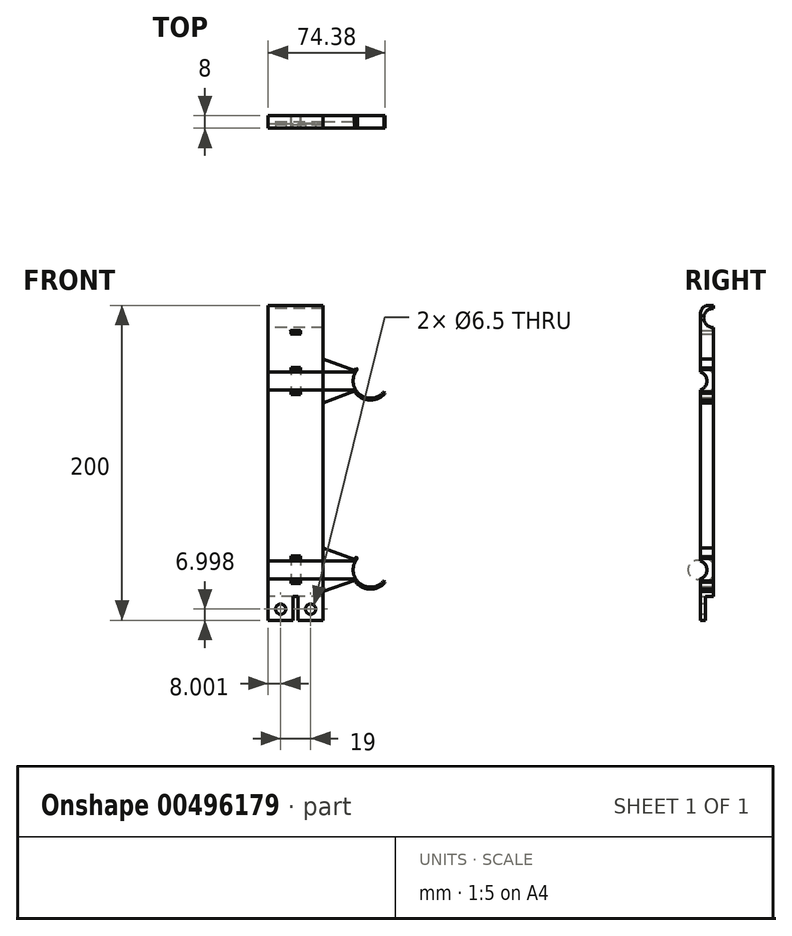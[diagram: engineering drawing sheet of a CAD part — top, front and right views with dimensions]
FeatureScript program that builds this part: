
annotation { "Feature Type Name" : "Feature", "Feature Type Description" : "" }
export const myFeature = defineFeature(function(context is Context, id is Id, definition is map)
    precondition{}
    {
        {
            var Q0;
            Q0=qCreatedBy(makeId("Front.planeOp"),FACE);
            var sketch = newSketch(context, id + "F0", { "sketchPlane" : qUnion([Q0])});
            skLineSegment(sketch, "E0.bottom", {"start": v(-13.38, 145.24) * mm, "end": v(21.62, 145.24) * mm});
            skLineSegment(sketch, "E0.top", {"start": v(-13.38, -54.76) * mm, "end": v(21.62, -54.76) * mm});
            skLineSegment(sketch, "E0.left", {"start": v(-13.38, 145.24) * mm, "end": v(-13.38, -54.76) * mm});
            skLineSegment(sketch, "E0.right", {"start": v(21.62, 145.24) * mm, "end": v(21.62, -54.76) * mm});
            skLineSegment(sketch, "E1", {"start": v(21.62, 145.24) * mm, "end": v(21.62, 137.24) * mm, "construction": true});
            skLineSegment(sketch, "E2", {"start": v(21.62, 137.24) * mm, "end": v(-13.38, 137.24) * mm, "construction": true});
            skSolve(sketch);
        }
        {
            var Q0;
            Q0=makeQuery(id+"F0.imprint","IMPRINT",FACE,{"disambiguationData":[TD([[makeQuery(id+"F0.imprint","IMPRINT",EDGE,{"derivedFrom":sQuery(id+"F0.wireOp",EDGE,"E0.bottom")}),-1.0]])]});
            extrude(context, id + "F1", {"entities" : qUnion([Q0]), "depth" : 8 * mm});
        }
        {
            var Q0;
            Q0=makeQuery(id+"F1.opExtrude","SWEPT_FACE",FACE,{"disambiguationData":[OSD([sQuery(id+"F0.wireOp",EDGE,"E0.left")])]});
            var sketch = newSketch(context, id + "F2", { "sketchPlane" : qUnion([Q0])});
            skLineSegment(sketch, "E3", {"start": v(0, 145.24) * mm, "end": v(0, 137.24) * mm, "construction": true});
            skLineSegment(sketch, "E4", {"start": v(0, 137.24) * mm, "end": v(-10.7, 137.24) * mm, "construction": true});
            skCircle(sketch, "E5", {"center": v(0, 137.24) * mm, "radius": 6.08 * mm, "construction": true});
            skCircle(sketch, "E6", {"center": v(0, 137.24) * mm, "radius": 6.08 * mm});
            skSolve(sketch);
        }
        {
            var Q0;
            Q0=qSketchRegion(id+"F2",true);
            extrude(context, id + "F3", {"entities" : qUnion([Q0]), "operationType" : NewBodyOperationType.REMOVE, "oppositeDirection" : true, "depth" : 45 * mm});
        }
        {
            var Q0;
            {var subQ0=sQuery(id+"F0.wireOp",EDGE,"E0.top");var subQ1=sQuery(id+"F0.wireOp",EDGE,"E0.left");var subQ2=sQuery(id+"F0.wireOp",EDGE,"E0.right");Q0=makeQuery(id+"F3.boolean.opBoolean","SPLIT",FACE,{"disambiguationData":[TD([makeQuery(id+"F1.opExtrude","SWEPT_FACE",FACE,{"disambiguationData":[OSD([subQ0])]})])],"derivedFrom":makeQuery(id+"F1.opExtrude","CAP_FACE",FACE,{"disambiguationData":[OSD([sQuery(id+"F0.wireOp",EDGE,"E0.bottom"),subQ0,subQ1,subQ2])],"isStart":true})});}
            var sketch = newSketch(context, id + "F4", { "sketchPlane" : qUnion([Q0])});
            skLineSegment(sketch, "E7", {"start": v(-4.12, 129.16) * mm, "end": v(-1.12, 129.16) * mm, "construction": true});
            skLineSegment(sketch, "E8", {"start": v(-1.12, 129.16) * mm, "end": v(-7.12, 129.16) * mm, "construction": true});
            skLineSegment(sketch, "E9.bottom", {"start": v(-7.12, 129.16) * mm, "end": v(-1.12, 129.16) * mm});
            skLineSegment(sketch, "E9.top", {"start": v(-7.12, 127.16) * mm, "end": v(-1.12, 127.16) * mm});
            skLineSegment(sketch, "E9.left", {"start": v(-7.12, 129.16) * mm, "end": v(-7.12, 127.16) * mm});
            skLineSegment(sketch, "E9.right", {"start": v(-1.12, 129.16) * mm, "end": v(-1.12, 127.16) * mm});
            skSolve(sketch);
        }
        {
            var Q0;
            Q0=makeQuery(id+"F4.imprint","IMPRINT",FACE,{"disambiguationData":[TD([[makeQuery(id+"F4.imprint","IMPRINT",EDGE,{"derivedFrom":sQuery(id+"F4.wireOp",EDGE,"E9.bottom")}),-1.0]])]});
            var sketch = newSketch(context, id + "F5", { "sketchPlane" : qUnion([Q0])});
            skSolve(sketch);
        }
        {
            var Q0;
            Q0=qSketchRegion(id+"F5",true);
            var Q1;
            Q1=makeQuery(id+"F4.imprint","IMPRINT",FACE,{"disambiguationData":[TD([[makeQuery(id+"F4.imprint","IMPRINT",EDGE,{"derivedFrom":sQuery(id+"F4.wireOp",EDGE,"E9.bottom")}),-1.0]])]});
            extrude(context, id + "F6", {"entities" : qUnion([Q0, Q1]), "operationType" : NewBodyOperationType.REMOVE, "oppositeDirection" : true, "depth" : 25 * mm});
        }
        {
            var Q0;
            Q0=makeQuery(id+"F6.boolean.opBoolean","INTERSECT",EDGE,{"derivedFrom":[makeQuery(id+"F1.opExtrude","CAP_FACE",FACE,{"disambiguationData":[OSD([sQuery(id+"F0.wireOp",EDGE,"E0.bottom"),sQuery(id+"F0.wireOp",EDGE,"E0.top"),sQuery(id+"F0.wireOp",EDGE,"E0.left"),sQuery(id+"F0.wireOp",EDGE,"E0.right")])],"isStart":false}),makeQuery(id+"F6.opExtrude","SWEPT_FACE",FACE,{"disambiguationData":[OSD([sQuery(id+"F4.wireOp",EDGE,"E9.bottom")])]})]});
            var Q1;
            Q1=makeQuery(id+"F6.boolean.opBoolean","INTERSECT",EDGE,{"derivedFrom":[makeQuery(id+"F1.opExtrude","CAP_FACE",FACE,{"disambiguationData":[OSD([sQuery(id+"F0.wireOp",EDGE,"E0.bottom"),sQuery(id+"F0.wireOp",EDGE,"E0.top"),sQuery(id+"F0.wireOp",EDGE,"E0.left"),sQuery(id+"F0.wireOp",EDGE,"E0.right")])],"isStart":false}),makeQuery(id+"F6.opExtrude","SWEPT_FACE",FACE,{"disambiguationData":[OSD([sQuery(id+"F4.wireOp",EDGE,"E9.top")])]})]});
            var Q2;
            Q2=makeQuery(id+"F6.boolean.opBoolean","INTERSECT",EDGE,{"derivedFrom":[makeQuery(id+"F1.opExtrude","CAP_FACE",FACE,{"disambiguationData":[OSD([sQuery(id+"F0.wireOp",EDGE,"E0.bottom"),sQuery(id+"F0.wireOp",EDGE,"E0.top"),sQuery(id+"F0.wireOp",EDGE,"E0.left"),sQuery(id+"F0.wireOp",EDGE,"E0.right")])],"isStart":false}),makeQuery(id+"F6.opExtrude","SWEPT_FACE",FACE,{"disambiguationData":[OSD([sQuery(id+"F4.wireOp",EDGE,"E9.left")])]})]});
            var Q3;
            Q3=makeQuery(id+"F6.boolean.opBoolean","INTERSECT",EDGE,{"derivedFrom":[makeQuery(id+"F1.opExtrude","CAP_FACE",FACE,{"disambiguationData":[OSD([sQuery(id+"F0.wireOp",EDGE,"E0.bottom"),sQuery(id+"F0.wireOp",EDGE,"E0.top"),sQuery(id+"F0.wireOp",EDGE,"E0.left"),sQuery(id+"F0.wireOp",EDGE,"E0.right")])],"isStart":false}),makeQuery(id+"F6.opExtrude","SWEPT_FACE",FACE,{"disambiguationData":[OSD([sQuery(id+"F4.wireOp",EDGE,"E9.right")])]})]});
            var Q4;
            Q4=makeQuery(id+"F6.boolean.opBoolean","COPY",EDGE,{"derivedFrom":makeQuery(id+"F6.opExtrude","CAP_EDGE",EDGE,{"disambiguationData":[OSD([sQuery(id+"F4.wireOp",EDGE,"E9.bottom")])],"isStart":true})});
            var Q5;
            Q5=makeQuery(id+"F6.boolean.opBoolean","COPY",EDGE,{"derivedFrom":makeQuery(id+"F6.opExtrude","CAP_EDGE",EDGE,{"disambiguationData":[OSD([sQuery(id+"F4.wireOp",EDGE,"E9.left")])],"isStart":true})});
            var Q6;
            Q6=makeQuery(id+"F6.boolean.opBoolean","COPY",EDGE,{"derivedFrom":makeQuery(id+"F6.opExtrude","CAP_EDGE",EDGE,{"disambiguationData":[OSD([sQuery(id+"F4.wireOp",EDGE,"E9.top")])],"isStart":true})});
            var Q7;
            Q7=makeQuery(id+"F6.boolean.opBoolean","COPY",EDGE,{"derivedFrom":makeQuery(id+"F6.opExtrude","CAP_EDGE",EDGE,{"disambiguationData":[OSD([sQuery(id+"F4.wireOp",EDGE,"E9.right")])],"isStart":true})});
            fillet(context, id + "F7", {"entities" : qUnion([Q0, Q1, Q2, Q3, Q4, Q5, Q6, Q7]), "radius" : 0.3 * mm, "tangentPropagation" : true, "allowEdgeOverflow" : false});
        }
        {
            var Q0;
            Q0=makeQuery(id+"F1.opExtrude","CAP_FACE",FACE,{"disambiguationData":[OSD([sQuery(id+"F0.wireOp",EDGE,"E0.bottom"),sQuery(id+"F0.wireOp",EDGE,"E0.top"),sQuery(id+"F0.wireOp",EDGE,"E0.left"),sQuery(id+"F0.wireOp",EDGE,"E0.right")])],"isStart":false});
            var sketch = newSketch(context, id + "F8", { "sketchPlane" : qUnion([Q0])});
            skLineSegment(sketch, "E10", {"start": v(-13.38, 145.24) * mm, "end": v(-13.38, -47.76) * mm, "construction": true});
            skLineSegment(sketch, "E11", {"start": v(-13.38, -47.76) * mm, "end": v(82.12, -47.76) * mm, "construction": true});
            skLineSegment(sketch, "E12", {"start": v(-13.38, -47.76) * mm, "end": v(21.62, -47.76) * mm, "construction": true});
            skLineSegment(sketch, "E13", {"start": v(21.62, -47.76) * mm, "end": v(13.62, -47.76) * mm, "construction": true});
            skLineSegment(sketch, "E14", {"start": v(13.62, -47.76) * mm, "end": v(13.62, -34.39) * mm, "construction": true});
            skLineSegment(sketch, "E15", {"start": v(-13.38, -47.76) * mm, "end": v(-5.38, -47.76) * mm, "construction": true});
            skLineSegment(sketch, "E16", {"start": v(-5.38, -43.12) * mm, "end": v(-5.38, -47.76) * mm, "construction": true});
            skCircle(sketch, "E17", {"center": v(-5.38, -47.76) * mm, "radius": 3.25 * mm});
            skCircle(sketch, "E18", {"center": v(13.62, -47.76) * mm, "radius": 3.25 * mm});
            skSolve(sketch);
        }
        {
            var Q0;
            Q0=qSketchRegion(id+"F8",true);
            extrude(context, id + "F9", {"entities" : qUnion([Q0]), "operationType" : NewBodyOperationType.REMOVE, "oppositeDirection" : true, "depth" : 25 * mm});
        }
        {
            var Q0;
            {var subQ0=sQuery(id+"F0.wireOp",EDGE,"E0.top");var subQ1=sQuery(id+"F0.wireOp",EDGE,"E0.left");var subQ2=sQuery(id+"F0.wireOp",EDGE,"E0.right");Q0=makeQuery(id+"F3.boolean.opBoolean","SPLIT",FACE,{"disambiguationData":[TD([makeQuery(id+"F1.opExtrude","SWEPT_FACE",FACE,{"disambiguationData":[OSD([subQ0])]})])],"derivedFrom":makeQuery(id+"F1.opExtrude","CAP_FACE",FACE,{"disambiguationData":[OSD([sQuery(id+"F0.wireOp",EDGE,"E0.bottom"),subQ0,subQ1,subQ2])],"isStart":true})});}
            var sketch = newSketch(context, id + "F10", { "sketchPlane" : qUnion([Q0])});
            skLineSegment(sketch, "E19.bottom", {"start": v(-21.62, -54.76) * mm, "end": v(13.38, -54.76) * mm});
            skLineSegment(sketch, "E19.top", {"start": v(-21.62, -39.76) * mm, "end": v(13.38, -39.76) * mm});
            skLineSegment(sketch, "E19.left", {"start": v(-21.62, -54.76) * mm, "end": v(-21.62, -39.76) * mm});
            skLineSegment(sketch, "E19.right", {"start": v(13.38, -54.76) * mm, "end": v(13.38, -39.76) * mm});
            skSolve(sketch);
        }
        {
            var Q0;
            Q0=makeQuery(id+"F10.imprint","IMPRINT",FACE,{"disambiguationData":[TD([[makeQuery(id+"F10.imprint","IMPRINT",EDGE,{"derivedFrom":sQuery(id+"F10.wireOp",EDGE,"E19.bottom")}),-1.0]])]});
            extrude(context, id + "F11", {"entities" : qUnion([Q0]), "operationType" : NewBodyOperationType.REMOVE, "oppositeDirection" : true, "depth" : 5 * mm});
        }
        {
            var Q0;
            Q0=makeQuery(id+"F11.boolean.opBoolean","COPY",FACE,{"derivedFrom":makeQuery(id+"F11.opExtrude","CAP_FACE",FACE,{"disambiguationData":[OSD([sQuery(id+"F0.wireOp",EDGE,"E0.bottom"),sQuery(id+"F0.wireOp",EDGE,"E0.top"),sQuery(id+"F0.wireOp",EDGE,"E0.left"),sQuery(id+"F0.wireOp",EDGE,"E0.right"),sQuery(id+"F8.wireOp",EDGE,"E17"),sQuery(id+"F8.wireOp",EDGE,"E18"),sQuery(id+"F10.wireOp",EDGE,"E19.bottom"),sQuery(id+"F10.wireOp",EDGE,"E19.top"),sQuery(id+"F10.wireOp",EDGE,"E19.left"),sQuery(id+"F10.wireOp",EDGE,"E19.right")])],"isStart":false})});
            var sketch = newSketch(context, id + "F12", { "sketchPlane" : qUnion([Q0])});
            skLineSegment(sketch, "E20", {"start": v(-21.62, -54.76) * mm, "end": v(-7.62, -54.76) * mm, "construction": true});
            skLineSegment(sketch, "E21", {"start": v(-5.72, -39.76) * mm, "end": v(-5.72, -54.76) * mm, "construction": true});
            skLineSegment(sketch, "E22", {"start": v(-2.52, -54.76) * mm, "end": v(-2.52, -39.76) * mm, "construction": true});
            skLineSegment(sketch, "E23.right", {"start": v(-5.72, -54.76) * mm, "end": v(-5.72, -39.76) * mm});
            skLineSegment(sketch, "E24.left", {"start": v(-2.52, -54.76) * mm, "end": v(-2.52, -39.76) * mm});
            skLineSegment(sketch, "E25.top", {"start": v(-2.52, -54.76) * mm, "end": v(-5.72, -54.76) * mm});
            skLineSegment(sketch, "E25.left", {"start": v(-2.52, -39.76) * mm, "end": v(-2.52, -54.76) * mm});
            skLineSegment(sketch, "E25.right", {"start": v(-5.72, -39.76) * mm, "end": v(-5.72, -54.76) * mm});
            skPoint(sketch, "E26.end.orphan", {"position": v(-0.62, -54.76) * mm});
            skLineSegment(sketch, "E27.top", {"start": v(-21.62, -54.76) * mm, "end": v(-5.72, -54.76) * mm});
            skLineSegment(sketch, "E28.bottom", {"start": v(-2.52, -39.76) * mm, "end": v(13.38, -39.76) * mm});
            skLineSegment(sketch, "E28.top", {"start": v(-2.52, -54.76) * mm, "end": v(-0.62, -54.76) * mm});
            skLineSegment(sketch, "E29.bottom", {"start": v(-5.72, -39.76) * mm, "end": v(-2.52, -39.76) * mm});
            skLineSegment(sketch, "E29.top", {"start": v(-5.72, -54.76) * mm, "end": v(-2.52, -54.76) * mm});
            skSolve(sketch);
        }
        {
            var Q0;
            Q0 = qSketchRegion(id + "F12", true);
            var Q1;
            {var subQ0=sQuery(id+"F0.wireOp",EDGE,"E0.top");var subQ1=sQuery(id+"F0.wireOp",EDGE,"E0.left");var subQ2=sQuery(id+"F0.wireOp",EDGE,"E0.right");Q1=makeQuery(id+"F3.boolean.opBoolean","SPLIT",FACE,{"disambiguationData":[TD([makeQuery(id+"F1.opExtrude","SWEPT_FACE",FACE,{"disambiguationData":[OSD([subQ0])]})])],"derivedFrom":makeQuery(id+"F1.opExtrude","CAP_FACE",FACE,{"disambiguationData":[OSD([sQuery(id+"F0.wireOp",EDGE,"E0.bottom"),subQ0,subQ1,subQ2])],"isStart":true})});}
            extrude(context, id + "F13", {"entities" : qUnion([Q0]), "operationType" : NewBodyOperationType.REMOVE, "oppositeDirection" : true, "endBoundEntityFace" : qUnion([Q1]), "depth" : 5 * mm});
        }
        {
            var Q0;
            Q0=makeQuery(id+"F1.opExtrude","CAP_FACE",FACE,{"disambiguationData":[OSD([sQuery(id+"F0.wireOp",EDGE,"E0.bottom"),sQuery(id+"F0.wireOp",EDGE,"E0.top"),sQuery(id+"F0.wireOp",EDGE,"E0.left"),sQuery(id+"F0.wireOp",EDGE,"E0.right")])],"isStart":false});
            var sketch = newSketch(context, id + "F14", { "sketchPlane" : qUnion([Q0])});
            skLineSegment(sketch, "E30", {"start": v(21.62, 145.24) * mm, "end": v(21.62, 97.24) * mm, "construction": true});
            skLineSegment(sketch, "E31", {"start": v(21.62, 97.24) * mm, "end": v(-44.16, 97.24) * mm, "construction": true});
            skLineSegment(sketch, "E32", {"start": v(21.62, 97.24) * mm, "end": v(51.62, 97.24) * mm, "construction": true});
            skLineSegment(sketch, "E33", {"start": v(51.62, 97.24) * mm, "end": v(51.62, 86.24) * mm, "construction": true});
            skArc(sketch, "E34", {"start": v(43.4, 104.54) * mm, "mid": v(44.46, 88.9) * mm, "end": v(60.09, 90.22) * mm, "construction": true});
            skArc(sketch, "E35.0", {"start": v(42.53, 105.29) * mm, "mid": v(41.92, 104.54) * mm, "end": v(41.37, 103.74) * mm});
            skLineSegment(sketch, "E36", {"start": v(41.37, 103.74) * mm, "end": v(21.62, 111.24) * mm});
            skLineSegment(sketch, "E37", {"start": v(21.62, 111.24) * mm, "end": v(21.62, 26.35) * mm});
            skArc(sketch, "E38", {"start": v(43.4, 104.54) * mm, "mid": v(44.46, 88.9) * mm, "end": v(60.09, 90.22) * mm});
            skLineSegment(sketch, "E39.MirrorCS", {"start": v(41.37, 90.74) * mm, "end": v(21.62, 83.24) * mm});
            skLineSegment(sketch, "E40", {"start": v(42.53, 105.29) * mm, "end": v(43.4, 104.54) * mm});
            skArc(sketch, "E41.trimOffspring", {"start": v(41.37, 90.74) * mm, "mid": v(50.84, 85.12) * mm, "end": v(60.96, 89.48) * mm});
            skLineSegment(sketch, "E42.trimOffspring", {"start": v(60.09, 90.22) * mm, "end": v(60.96, 89.48) * mm});
            skSolve(sketch);
        }
        {
            var Q0;
            Q0=makeQuery(id+"F14.imprint","IMPRINT",FACE,{"disambiguationData":[TD([[makeQuery(id+"F14.imprint","IMPRINT",EDGE,{"derivedFrom":sQuery(id+"F14.wireOp",EDGE,"E35.0")}),1.0]])]});
            extrude(context, id + "F15", {"entities" : qUnion([Q0]), "oppositeDirection" : true, "depth" : 8 * mm});
        }
        {
            var Q0;
            Q0=makeQuery(id+"F1.opExtrude","SWEPT_FACE",FACE,{"disambiguationData":[OSD([sQuery(id+"F0.wireOp",EDGE,"E0.left")])]});
            var sketch = newSketch(context, id + "F16", { "sketchPlane" : qUnion([Q0])});
            skLineSegment(sketch, "E43", {"start": v(10, 97.24) * mm, "end": v(37.36, 97.24) * mm, "construction": true});
            skCircle(sketch, "E44", {"center": v(10, 97.24) * mm, "radius": 6 * mm});
            skSolve(sketch);
        }
        {
            var Q0;
            {var subQ0=sQuery(id+"F16.wireOp",EDGE,"E44");var subQ1=makeQuery(id+"F1.opExtrude","CAP_EDGE",EDGE,{"disambiguationData":[OSD([sQuery(id+"F0.wireOp",EDGE,"E0.left")])],"isStart":false});var subQ2=makeQuery(id+"F16.imprint","INTERSECT",VERTEX,{"disambiguationData":[OD(0.0)],"derivedFrom":[subQ1,subQ0]});Q0=makeQuery(id+"F16.imprint","IMPRINT",FACE,{"disambiguationData":[TD([[makeQuery(id+"F16.imprint","IMPRINT",EDGE,{"disambiguationData":[TD([[subQ2,-1.0]])],"derivedFrom":subQ0}),1.0]])]});}
            var Q1;
            Q1=makeQuery(id+"F15.opExtrude","SWEPT_FACE",FACE,{"disambiguationData":[OSD([sQuery(id+"F14.wireOp",EDGE,"E38")])]});
            extrude(context, id + "F17", {"entities" : qUnion([Q0]), "operationType" : NewBodyOperationType.REMOVE, "oppositeDirection" : true, "endBoundEntityFace" : qUnion([Q1]), "depth" : 60 * mm});
        }
        {
            var Q0;
            {var subQ0=sQuery(id+"F0.wireOp",EDGE,"E0.right");var subQ1=sQuery(id+"F0.wireOp",EDGE,"E0.left");var subQ2=sQuery(id+"F0.wireOp",EDGE,"E0.top");Q0=makeQuery(id+"F17.boolean.opBoolean","SPLIT",FACE,{"disambiguationData":[TD([makeQuery(id+"F1.opExtrude","SWEPT_FACE",FACE,{"disambiguationData":[OSD([subQ2])]})])],"derivedFrom":makeQuery(id+"F1.opExtrude","CAP_FACE",FACE,{"disambiguationData":[OSD([sQuery(id+"F0.wireOp",EDGE,"E0.bottom"),subQ2,subQ1,subQ0])],"isStart":false})});}
            var sketch = newSketch(context, id + "F18", { "sketchPlane" : qUnion([Q0])});
            skLineSegment(sketch, "E45.bottom", {"start": v(1.12, 105.9) * mm, "end": v(7.12, 105.9) * mm});
            skLineSegment(sketch, "E45.top", {"start": v(1.12, 103.9) * mm, "end": v(7.12, 103.9) * mm});
            skLineSegment(sketch, "E45.left", {"start": v(1.12, 105.9) * mm, "end": v(1.12, 103.9) * mm});
            skLineSegment(sketch, "E45.right", {"start": v(7.12, 105.9) * mm, "end": v(7.12, 103.9) * mm});
            skLineSegment(sketch, "E46.bottom", {"start": v(1.12, 90.58) * mm, "end": v(7.12, 90.58) * mm});
            skLineSegment(sketch, "E46.top", {"start": v(1.12, 88.58) * mm, "end": v(7.12, 88.58) * mm});
            skLineSegment(sketch, "E46.left", {"start": v(1.12, 90.58) * mm, "end": v(1.12, 88.58) * mm});
            skLineSegment(sketch, "E46.right", {"start": v(7.12, 90.58) * mm, "end": v(7.12, 88.58) * mm});
            skSolve(sketch);
        }
        {
            var Q0;
            Q0=makeQuery(id+"F18.imprint","IMPRINT",FACE,{"disambiguationData":[TD([[makeQuery(id+"F18.imprint","IMPRINT",EDGE,{"derivedFrom":sQuery(id+"F18.wireOp",EDGE,"E45.bottom")}),-1.0]])]});
            var Q1;
            Q1=makeQuery(id+"F18.imprint","IMPRINT",FACE,{"disambiguationData":[TD([[makeQuery(id+"F18.imprint","IMPRINT",EDGE,{"derivedFrom":sQuery(id+"F18.wireOp",EDGE,"E46.bottom")}),-1.0]])]});
            extrude(context, id + "F19", {"entities" : qUnion([Q0, Q1]), "operationType" : NewBodyOperationType.REMOVE, "oppositeDirection" : true, "depth" : 25 * mm});
        }
        {
            var Q0;
            {var subQ0=sQuery(id+"F0.wireOp",EDGE,"E0.top");var subQ1=sQuery(id+"F0.wireOp",EDGE,"E0.left");var subQ2=sQuery(id+"F0.wireOp",EDGE,"E0.right");Q0=makeQuery(id+"F19.boolean.opBoolean","INTERSECT",EDGE,{"derivedFrom":[makeQuery(id+"F3.boolean.opBoolean","SPLIT",FACE,{"disambiguationData":[TD([makeQuery(id+"F1.opExtrude","SWEPT_FACE",FACE,{"disambiguationData":[OSD([subQ0])]})])],"derivedFrom":makeQuery(id+"F1.opExtrude","CAP_FACE",FACE,{"disambiguationData":[OSD([sQuery(id+"F0.wireOp",EDGE,"E0.bottom"),subQ0,subQ1,subQ2])],"isStart":true})}),makeQuery(id+"F19.opExtrude","SWEPT_FACE",FACE,{"disambiguationData":[OSD([sQuery(id+"F18.wireOp",EDGE,"E45.top")])]})]});}
            var Q1;
            {var subQ0=sQuery(id+"F0.wireOp",EDGE,"E0.top");var subQ1=sQuery(id+"F0.wireOp",EDGE,"E0.left");var subQ2=sQuery(id+"F0.wireOp",EDGE,"E0.right");Q1=makeQuery(id+"F19.boolean.opBoolean","INTERSECT",EDGE,{"derivedFrom":[makeQuery(id+"F3.boolean.opBoolean","SPLIT",FACE,{"disambiguationData":[TD([makeQuery(id+"F1.opExtrude","SWEPT_FACE",FACE,{"disambiguationData":[OSD([subQ0])]})])],"derivedFrom":makeQuery(id+"F1.opExtrude","CAP_FACE",FACE,{"disambiguationData":[OSD([sQuery(id+"F0.wireOp",EDGE,"E0.bottom"),subQ0,subQ1,subQ2])],"isStart":true})}),makeQuery(id+"F19.opExtrude","SWEPT_FACE",FACE,{"disambiguationData":[OSD([sQuery(id+"F18.wireOp",EDGE,"E46.bottom")])]})]});}
            fillet(context, id + "F20", {"entities" : qUnion([Q0, Q1]), "radius" : 3 * mm, "tangentPropagation" : true, "allowEdgeOverflow" : false});
        }
        {
            var Q0;
            {var subQ0=sQuery(id+"F0.wireOp",EDGE,"E0.left");var subQ1=sQuery(id+"F0.wireOp",EDGE,"E0.right");var subQ2=sQuery(id+"F0.wireOp",EDGE,"E0.top");var subQ3=sQuery(id+"F0.wireOp",EDGE,"E0.bottom");Q0=makeQuery(id+"F17.boolean.opBoolean","SPLIT",FACE,{"disambiguationData":[TD([makeQuery(id+"F1.opExtrude","SWEPT_FACE",FACE,{"disambiguationData":[OSD([subQ3])]})])],"derivedFrom":makeQuery(id+"F1.opExtrude","CAP_FACE",FACE,{"disambiguationData":[OSD([subQ3,subQ2,subQ0,subQ1])],"isStart":false})});}
            var sketch = newSketch(context, id + "F21", { "sketchPlane" : qUnion([Q0])});
            skLineSegment(sketch, "E47", {"start": v(21.62, 145.24) * mm, "end": v(21.62, -22.76) * mm, "construction": true});
            skLineSegment(sketch, "E48", {"start": v(21.62, -22.76) * mm, "end": v(-13.38, -22.76) * mm, "construction": true});
            skLineSegment(sketch, "E49", {"start": v(21.62, -22.78) * mm, "end": v(51.62, -22.78) * mm, "construction": true});
            skLineSegment(sketch, "E50", {"start": v(51.62, -22.78) * mm, "end": v(51.62, -33.78) * mm, "construction": true});
            skArc(sketch, "E51", {"start": v(43.4, -15.47) * mm, "mid": v(44.46, -31.12) * mm, "end": v(60.09, -29.8) * mm, "construction": true});
            skArc(sketch, "E52.0", {"start": v(42.49, -14.69) * mm, "mid": v(41.9, -15.4) * mm, "end": v(41.37, -16.17) * mm});
            skLineSegment(sketch, "E53", {"start": v(41.37, -16.17) * mm, "end": v(21.62, -8.94) * mm});
            skLineSegment(sketch, "E54", {"start": v(21.62, -8.94) * mm, "end": v(21.62, -43.66) * mm});
            skArc(sketch, "E55", {"start": v(43.4, -15.47) * mm, "mid": v(44.46, -31.12) * mm, "end": v(60.09, -29.8) * mm});
            skLineSegment(sketch, "E56.MirrorCS", {"start": v(41.37, -29.39) * mm, "end": v(21.62, -36.62) * mm});
            skLineSegment(sketch, "E57", {"start": v(42.49, -14.69) * mm, "end": v(43.4, -15.47) * mm});
            skArc(sketch, "E58.trimOffspring", {"start": v(41.37, -29.39) * mm, "mid": v(50.88, -34.95) * mm, "end": v(61, -30.58) * mm});
            skLineSegment(sketch, "E59.trimOffspring", {"start": v(60.09, -29.8) * mm, "end": v(61, -30.58) * mm});
            skSolve(sketch);
        }
        {
            var Q0;
            Q0=makeQuery(id+"F21.imprint","IMPRINT",FACE,{"disambiguationData":[TD([[makeQuery(id+"F21.imprint","IMPRINT",EDGE,{"derivedFrom":sQuery(id+"F21.wireOp",EDGE,"E52.0")}),1.0]])]});
            extrude(context, id + "F22", {"entities" : qUnion([Q0]), "oppositeDirection" : true, "depth" : 8 * mm});
        }
        {
            var Q0;
            Q0=makeQuery(id+"F1.opExtrude","SWEPT_FACE",FACE,{"disambiguationData":[OSD([sQuery(id+"F0.wireOp",EDGE,"E0.left")])]});
            var sketch = newSketch(context, id + "F23", { "sketchPlane" : qUnion([Q0])});
            skCircle(sketch, "E60", {"center": v(10, -22.76) * mm, "radius": 6 * mm});
            skSolve(sketch);
        }
        {
            var Q0;
            {var subQ0=sQuery(id+"F23.wireOp",EDGE,"E60");var subQ1=sQuery(id+"F0.wireOp",EDGE,"E0.left");var subQ2=sQuery(id+"F0.wireOp",EDGE,"E0.top");var subQ3=makeQuery(id+"F17.boolean.opBoolean","SPLIT",EDGE,{"disambiguationData":[TD([makeQuery(id+"F1.opExtrude","SWEPT_FACE",FACE,{"disambiguationData":[OSD([subQ2])]})])],"derivedFrom":makeQuery(id+"F1.opExtrude","CAP_EDGE",EDGE,{"disambiguationData":[OSD([subQ1])],"isStart":false})});var subQ4=makeQuery(id+"F23.imprint","INTERSECT",VERTEX,{"disambiguationData":[OD(0.0)],"derivedFrom":[subQ3,subQ0]});Q0=makeQuery(id+"F23.imprint","IMPRINT",FACE,{"disambiguationData":[TD([[makeQuery(id+"F23.imprint","IMPRINT",EDGE,{"disambiguationData":[TD([[subQ4,1.0]])],"derivedFrom":subQ0}),1.0]])]});}
            extrude(context, id + "F24", {"entities" : qUnion([Q0]), "operationType" : NewBodyOperationType.REMOVE, "oppositeDirection" : true, "depth" : 60 * mm});
        }
        {
            var Q0;
            {var subQ0=sQuery(id+"F0.wireOp",EDGE,"E0.right");var subQ1=sQuery(id+"F0.wireOp",EDGE,"E0.left");var subQ2=sQuery(id+"F0.wireOp",EDGE,"E0.top");var subQ3=makeQuery(id+"F1.opExtrude","CAP_FACE",FACE,{"disambiguationData":[OSD([sQuery(id+"F0.wireOp",EDGE,"E0.bottom"),subQ2,subQ1,subQ0])],"isStart":false});Q0=makeQuery(id+"F24.boolean.opBoolean","SPLIT",FACE,{"disambiguationData":[TD([makeQuery(id+"F19.boolean.opBoolean","COPY",FACE,{"derivedFrom":makeQuery(id+"F19.opExtrude","SWEPT_FACE",FACE,{"disambiguationData":[OSD([sQuery(id+"F18.wireOp",EDGE,"E46.bottom")])]})})])],"derivedFrom":makeQuery(id+"F17.boolean.opBoolean","SPLIT",FACE,{"disambiguationData":[TD([makeQuery(id+"F1.opExtrude","SWEPT_FACE",FACE,{"disambiguationData":[OSD([subQ2])]})])],"derivedFrom":subQ3})});}
            var sketch = newSketch(context, id + "F25", { "sketchPlane" : qUnion([Q0])});
            skLineSegment(sketch, "E61.bottom", {"start": v(1.12, -14.1) * mm, "end": v(7.12, -14.1) * mm});
            skLineSegment(sketch, "E61.top", {"start": v(1.12, -16.1) * mm, "end": v(7.12, -16.1) * mm});
            skLineSegment(sketch, "E61.left", {"start": v(1.12, -14.1) * mm, "end": v(1.12, -16.1) * mm});
            skLineSegment(sketch, "E61.right", {"start": v(7.12, -14.1) * mm, "end": v(7.12, -16.1) * mm});
            skLineSegment(sketch, "E62.bottom", {"start": v(1.12, -29.42) * mm, "end": v(7.12, -29.42) * mm});
            skLineSegment(sketch, "E62.top", {"start": v(1.12, -31.42) * mm, "end": v(7.12, -31.42) * mm});
            skLineSegment(sketch, "E62.left", {"start": v(1.12, -29.42) * mm, "end": v(1.12, -31.42) * mm});
            skLineSegment(sketch, "E62.right", {"start": v(7.12, -29.42) * mm, "end": v(7.12, -31.42) * mm});
            skSolve(sketch);
        }
        {
            var Q0;
            Q0=makeQuery(id+"F25.imprint","IMPRINT",FACE,{"disambiguationData":[TD([[makeQuery(id+"F25.imprint","IMPRINT",EDGE,{"derivedFrom":sQuery(id+"F25.wireOp",EDGE,"E61.bottom")}),-1.0]])]});
            var Q1;
            Q1=makeQuery(id+"F25.imprint","IMPRINT",FACE,{"disambiguationData":[TD([[makeQuery(id+"F25.imprint","IMPRINT",EDGE,{"derivedFrom":sQuery(id+"F25.wireOp",EDGE,"E62.bottom")}),-1.0]])]});
            extrude(context, id + "F26", {"entities" : qUnion([Q0, Q1]), "operationType" : NewBodyOperationType.REMOVE, "oppositeDirection" : true, "depth" : 25 * mm});
        }
        {
            var Q0;
            {var subQ0=sQuery(id+"F0.wireOp",EDGE,"E0.top");var subQ1=sQuery(id+"F0.wireOp",EDGE,"E0.left");var subQ2=sQuery(id+"F0.wireOp",EDGE,"E0.right");Q0=makeQuery(id+"F26.boolean.opBoolean","INTERSECT",EDGE,{"derivedFrom":[makeQuery(id+"F3.boolean.opBoolean","SPLIT",FACE,{"disambiguationData":[TD([makeQuery(id+"F1.opExtrude","SWEPT_FACE",FACE,{"disambiguationData":[OSD([subQ0])]})])],"derivedFrom":makeQuery(id+"F1.opExtrude","CAP_FACE",FACE,{"disambiguationData":[OSD([sQuery(id+"F0.wireOp",EDGE,"E0.bottom"),subQ0,subQ1,subQ2])],"isStart":true})}),makeQuery(id+"F26.opExtrude","SWEPT_FACE",FACE,{"disambiguationData":[OSD([sQuery(id+"F25.wireOp",EDGE,"E61.top")])]})]});}
            var Q1;
            {var subQ0=sQuery(id+"F0.wireOp",EDGE,"E0.top");var subQ1=sQuery(id+"F0.wireOp",EDGE,"E0.left");var subQ2=sQuery(id+"F0.wireOp",EDGE,"E0.right");Q1=makeQuery(id+"F26.boolean.opBoolean","INTERSECT",EDGE,{"derivedFrom":[makeQuery(id+"F3.boolean.opBoolean","SPLIT",FACE,{"disambiguationData":[TD([makeQuery(id+"F1.opExtrude","SWEPT_FACE",FACE,{"disambiguationData":[OSD([subQ0])]})])],"derivedFrom":makeQuery(id+"F1.opExtrude","CAP_FACE",FACE,{"disambiguationData":[OSD([sQuery(id+"F0.wireOp",EDGE,"E0.bottom"),subQ0,subQ1,subQ2])],"isStart":true})}),makeQuery(id+"F26.opExtrude","SWEPT_FACE",FACE,{"disambiguationData":[OSD([sQuery(id+"F25.wireOp",EDGE,"E62.bottom")])]})]});}
            fillet(context, id + "F27", {"entities" : qUnion([Q0, Q1]), "radius" : 4 * mm, "tangentPropagation" : true, "allowEdgeOverflow" : false});
        }
        {
            var Q0;
            Q0=makeQuery(id+"F1.opExtrude","CAP_EDGE",EDGE,{"disambiguationData":[OSD([sQuery(id+"F0.wireOp",EDGE,"E0.bottom")])],"isStart":false});
            fillet(context, id + "F28", {"entities" : qUnion([Q0]), "radius" : 5 * mm, "tangentPropagation" : true, "allowEdgeOverflow" : false});
        }
    });
